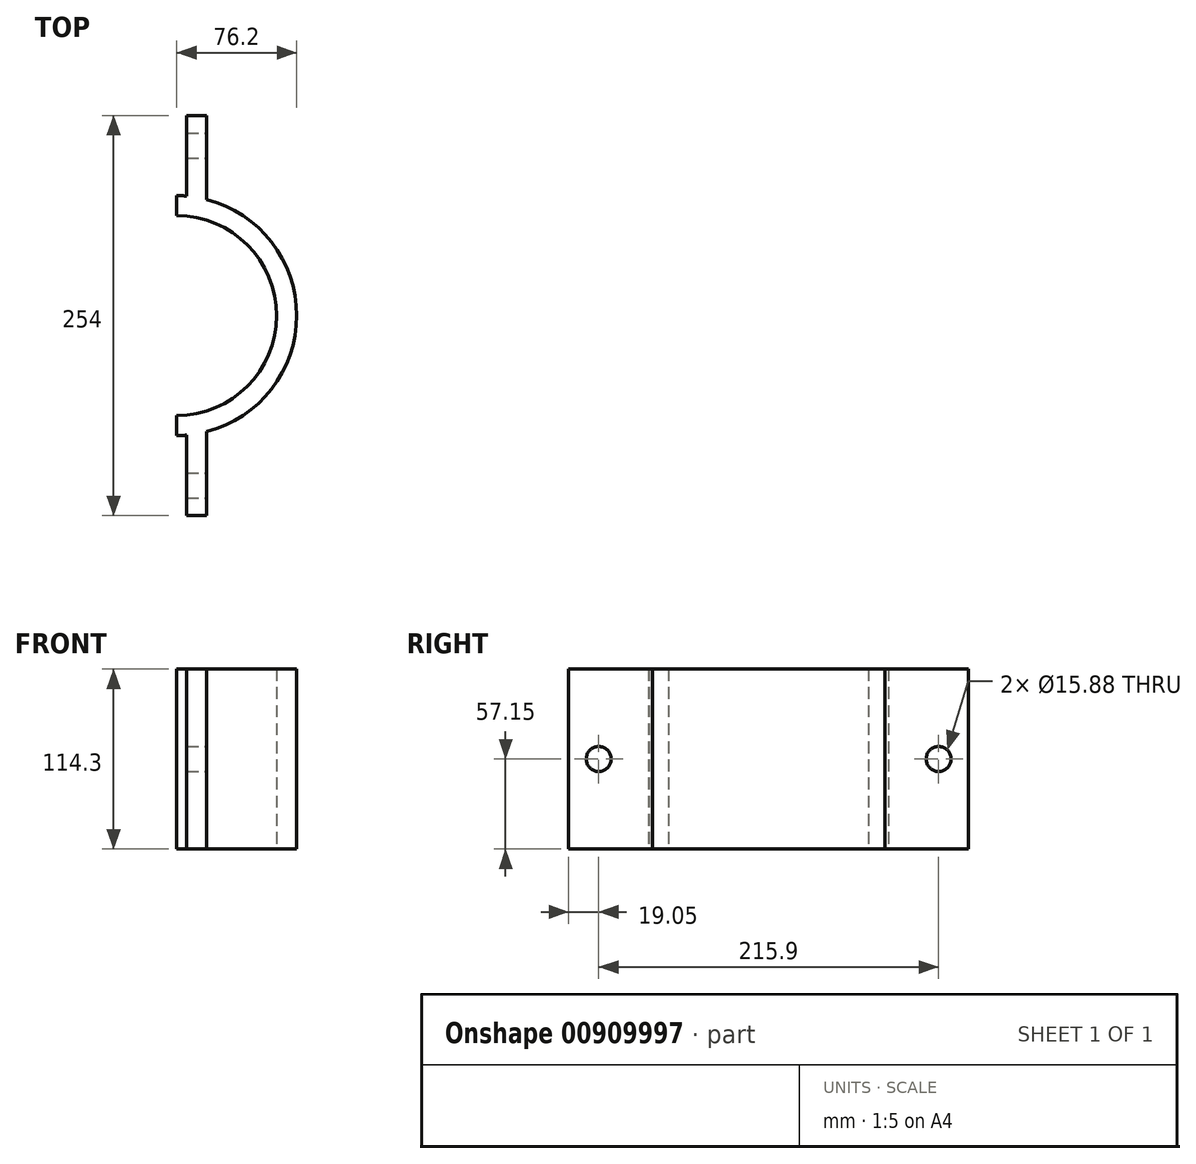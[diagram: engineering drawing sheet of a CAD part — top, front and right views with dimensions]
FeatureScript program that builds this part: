
annotation { "Feature Type Name" : "Feature", "Feature Type Description" : "" }
export const myFeature = defineFeature(function(context is Context, id is Id, definition is map)
    precondition{}
    {
        {
            var Q0;
            Q0=qCreatedBy(makeId("Top.planeOp"),FACE);
            var sketch = newSketch(context, id + "F0", { "sketchPlane" : qUnion([Q0])});
            skArc(sketch, "E0", {"start": v(0, -63.5) * mm, "mid": v(63.5, 0) * mm, "end": v(0, 63.5) * mm});
            skArc(sketch, "E1", {"start": v(0, -76.2) * mm, "mid": v(3.18, -76.13) * mm, "end": v(6.35, -75.93) * mm});
            skLineSegment(sketch, "E2.bottom", {"start": v(6.35, 127) * mm, "end": v(19.05, 127) * mm});
            skLineSegment(sketch, "E2.top", {"start": v(6.35, -127) * mm, "end": v(19.05, -127) * mm});
            skLineSegment(sketch, "E2.left", {"start": v(6.35, 127) * mm, "end": v(6.35, 75.93) * mm});
            skLineSegment(sketch, "E2.right", {"start": v(19.05, 127) * mm, "end": v(19.05, 73.78) * mm});
            skLineSegment(sketch, "E3", {"start": v(0, 76.2) * mm, "end": v(0, 63.5) * mm});
            skPoint(sketch, "E4.orphan", {"position": v(0, 95.48) * mm});
            skLineSegment(sketch, "E5.trimOffspring", {"start": v(0, -63.5) * mm, "end": v(0, -76.2) * mm});
            skLineSegment(sketch, "E6.trimOffspring", {"start": v(6.35, -75.93) * mm, "end": v(6.35, -127) * mm});
            skLineSegment(sketch, "E7.trimOffspring", {"start": v(19.05, -73.78) * mm, "end": v(19.05, -127) * mm});
            skArc(sketch, "E8.trimOffspring", {"start": v(19.05, -73.78) * mm, "mid": v(76.2, 0) * mm, "end": v(19.05, 73.78) * mm});
            skArc(sketch, "E9.trimOffspring", {"start": v(6.35, 75.93) * mm, "mid": v(3.18, 76.13) * mm, "end": v(0, 76.2) * mm});
            skSolve(sketch);
        }
        {
            var Q0;
            Q0=makeQuery(id+"F0.imprint","IMPRINT",FACE,{"disambiguationData":[TD([[makeQuery(id+"F0.imprint","IMPRINT",EDGE,{"derivedFrom":sQuery(id+"F0.wireOp",EDGE,"E0")}),-1.0]])]});
            extrude(context, id + "F1", {"entities" : qUnion([Q0]), "depth" : 114.3 * mm, "offsetDistance" : 25 * mm});
        }
        {
            var Q0;
            Q0=makeQuery(id+"F1.opExtrude","SWEPT_FACE",FACE,{"disambiguationData":[OSD([sQuery(id+"F0.wireOp",EDGE,"E7.trimOffspring")])]});
            var sketch = newSketch(context, id + "F2", { "sketchPlane" : qUnion([Q0])});
            skLineSegment(sketch, "E10", {"start": v(-107.95, 57.15) * mm, "end": v(107.95, 57.15) * mm, "construction": true});
            skPoint(sketch, "E10.startSnap0", {"position": v(-127, 57.15) * mm});
            skCircle(sketch, "E11", {"center": v(-107.95, 57.15) * mm, "radius": 7.94 * mm});
            skCircle(sketch, "E12", {"center": v(107.95, 57.15) * mm, "radius": 7.94 * mm});
            skPoint(sketch, "E13", {"position": v(0, 57.15) * mm});
            skSolve(sketch);
        }
        {
            var Q0;
            Q0=makeQuery(id+"F2.imprint","IMPRINT",FACE,{"disambiguationData":[TD([[makeQuery(id+"F2.imprint","IMPRINT",EDGE,{"derivedFrom":sQuery(id+"F2.wireOp",EDGE,"E11")}),1.0]])]});
            var Q1;
            Q1=makeQuery(id+"F2.imprint","IMPRINT",FACE,{"disambiguationData":[TD([[makeQuery(id+"F2.imprint","IMPRINT",EDGE,{"derivedFrom":sQuery(id+"F2.wireOp",EDGE,"E12")}),1.0]])]});
            extrude(context, id + "F3", {"entities" : qUnion([Q0, Q1]), "operationType" : NewBodyOperationType.REMOVE, "endBound" : BoundingType.THROUGH_ALL, "oppositeDirection" : true, "depth" : 25 * mm, "offsetDistance" : 25 * mm});
        }
    });
